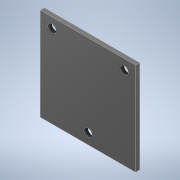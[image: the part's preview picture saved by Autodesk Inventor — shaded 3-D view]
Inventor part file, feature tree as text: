
AUTODESK INVENTOR PART (.ipt)
format: ipt  version: 2022 (Build 260153000, 153)  size: 102,912 bytes
history: native  units: mm
features: other x1, extrude x1, sketch x1
ambient origin geometry x8: Origin, YZ Plane, XZ Plane, XY Plane, X Axis, Y Axis, Z Axis, Center Point
bodies: Body1 (feature_tree)
feature tree (3):
  other  "ソリッド1"
  extrude  "押し出し1"  Depth=37.0mm
  sketch  "スケッチ1"
